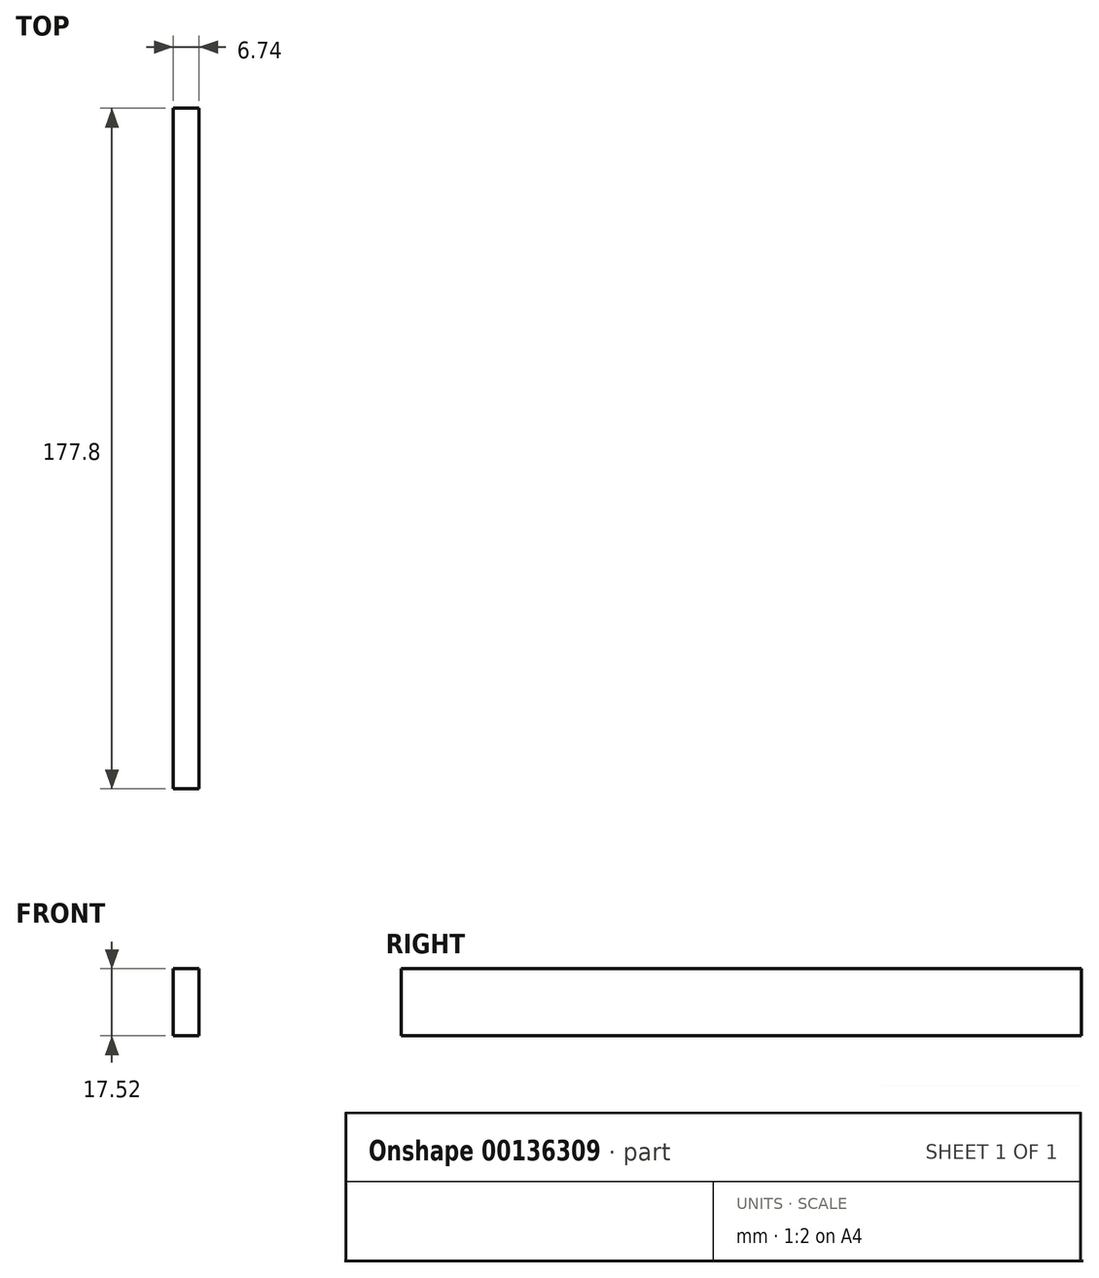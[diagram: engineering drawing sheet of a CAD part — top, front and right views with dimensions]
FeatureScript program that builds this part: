
annotation { "Feature Type Name" : "Feature", "Feature Type Description" : "" }
export const myFeature = defineFeature(function(context is Context, id is Id, definition is map)
    precondition{}
    {
        {
            var Q0;
            Q0=qCreatedBy(makeId("Front.planeOp"),FACE);
            var sketch = newSketch(context, id + "F0", { "sketchPlane" : qUnion([Q0])});
            skLineSegment(sketch, "E0.bottom", {"start": v(-3.37, 8.76) * mm, "end": v(3.37, 8.76) * mm});
            skLineSegment(sketch, "E0.top", {"start": v(-3.37, -8.76) * mm, "end": v(3.37, -8.76) * mm});
            skLineSegment(sketch, "E0.left", {"start": v(-3.37, 8.76) * mm, "end": v(-3.37, -8.76) * mm});
            skLineSegment(sketch, "E0.right", {"start": v(3.37, 8.76) * mm, "end": v(3.37, -8.76) * mm});
            skPoint(sketch, "E0.middle", {"position": v(0, 0) * mm});
            skSolve(sketch);
        }
        {
            var Q0;
            Q0=makeQuery(id+"F0.imprint","IMPRINT",FACE,{"disambiguationData":[TD([[makeQuery(id+"F0.imprint","IMPRINT",EDGE,{"derivedFrom":sQuery(id+"F0.wireOp",EDGE,"E0.bottom")}),-1.0]])]});
            extrude(context, id + "F1", {"entities" : qUnion([Q0]), "depth" : 177.8 * mm});
        }
    });
